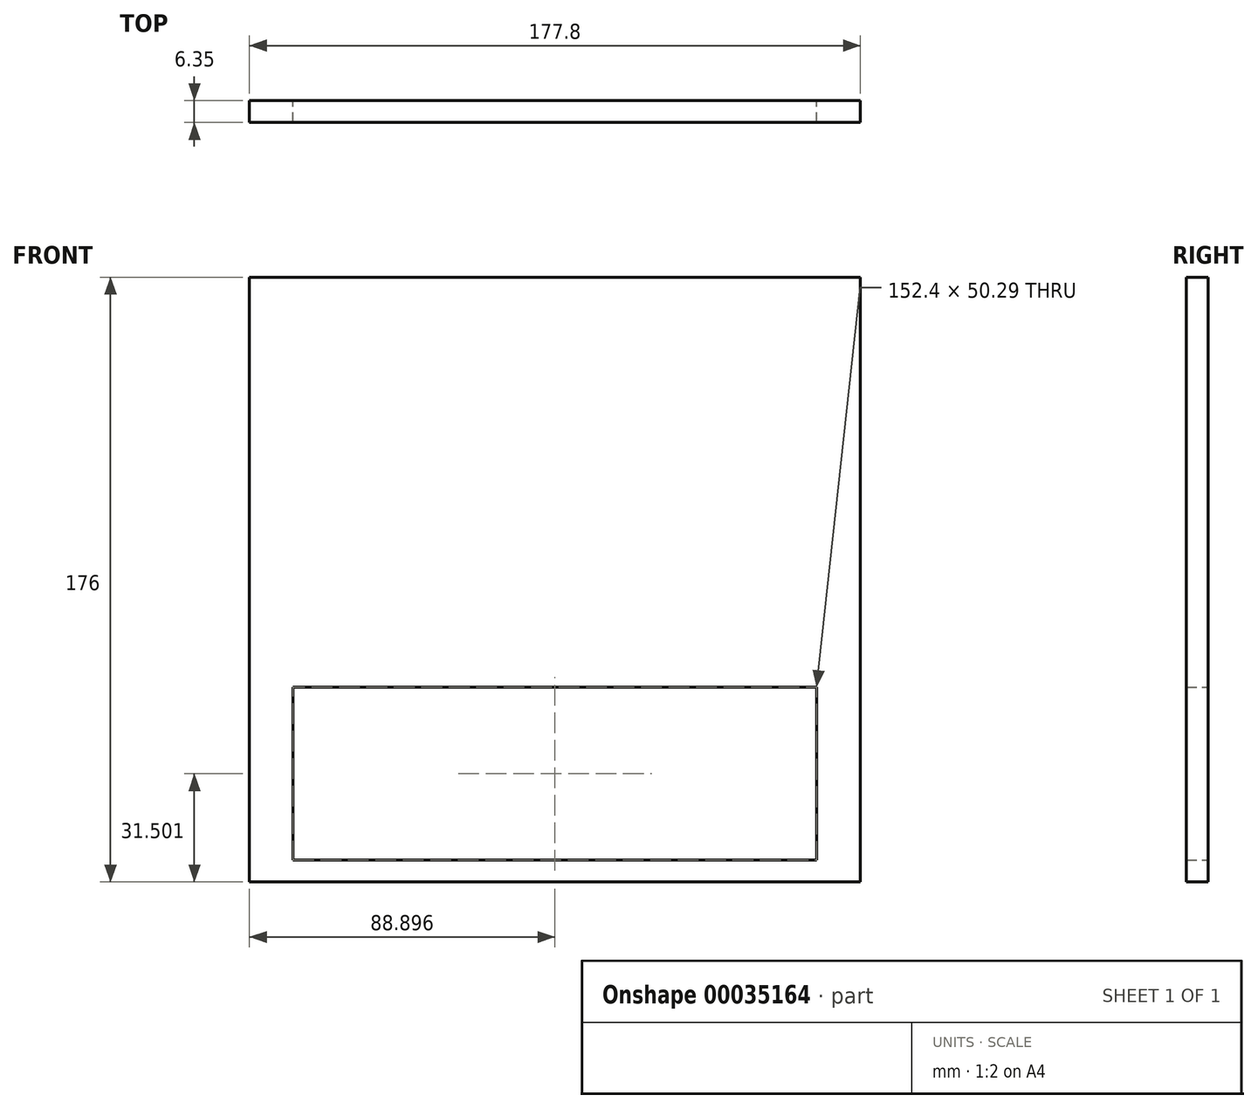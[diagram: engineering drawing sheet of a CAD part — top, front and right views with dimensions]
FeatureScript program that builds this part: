
annotation { "Feature Type Name" : "Feature", "Feature Type Description" : "" }
export const myFeature = defineFeature(function(context is Context, id is Id, definition is map)
    precondition{}
    {
        {
            var Q0;
            Q0=qCreatedBy(makeId("Front.planeOp"),FACE);
            var sketch = newSketch(context, id + "F0", { "sketchPlane" : qUnion([Q0])});
            skLineSegment(sketch, "E0.bottom", {"start": v(-73.72, 88.78) * mm, "end": v(104.08, 88.78) * mm});
            skLineSegment(sketch, "E0.top", {"start": v(-73.72, -87.22) * mm, "end": v(104.08, -87.22) * mm});
            skLineSegment(sketch, "E0.left", {"start": v(-73.72, 88.78) * mm, "end": v(-73.72, -87.22) * mm});
            skLineSegment(sketch, "E0.right", {"start": v(104.08, 88.78) * mm, "end": v(104.08, -87.22) * mm});
            skLineSegment(sketch, "E1.bottom", {"start": v(-61.02, -30.57) * mm, "end": v(91.38, -30.57) * mm});
            skLineSegment(sketch, "E1.top", {"start": v(-61.02, -80.87) * mm, "end": v(91.38, -80.87) * mm});
            skLineSegment(sketch, "E1.left", {"start": v(-61.02, -30.57) * mm, "end": v(-61.02, -80.87) * mm});
            skLineSegment(sketch, "E1.right", {"start": v(91.38, -30.57) * mm, "end": v(91.38, -80.87) * mm});
            skSolve(sketch);
        }
        {
            var Q0;
            Q0 = qSketchRegion(id + "F0", true);
            extrude(context, id + "F1", {"entities" : qUnion([Q0]), "depth" : 6.35 * mm});
        }
    });
